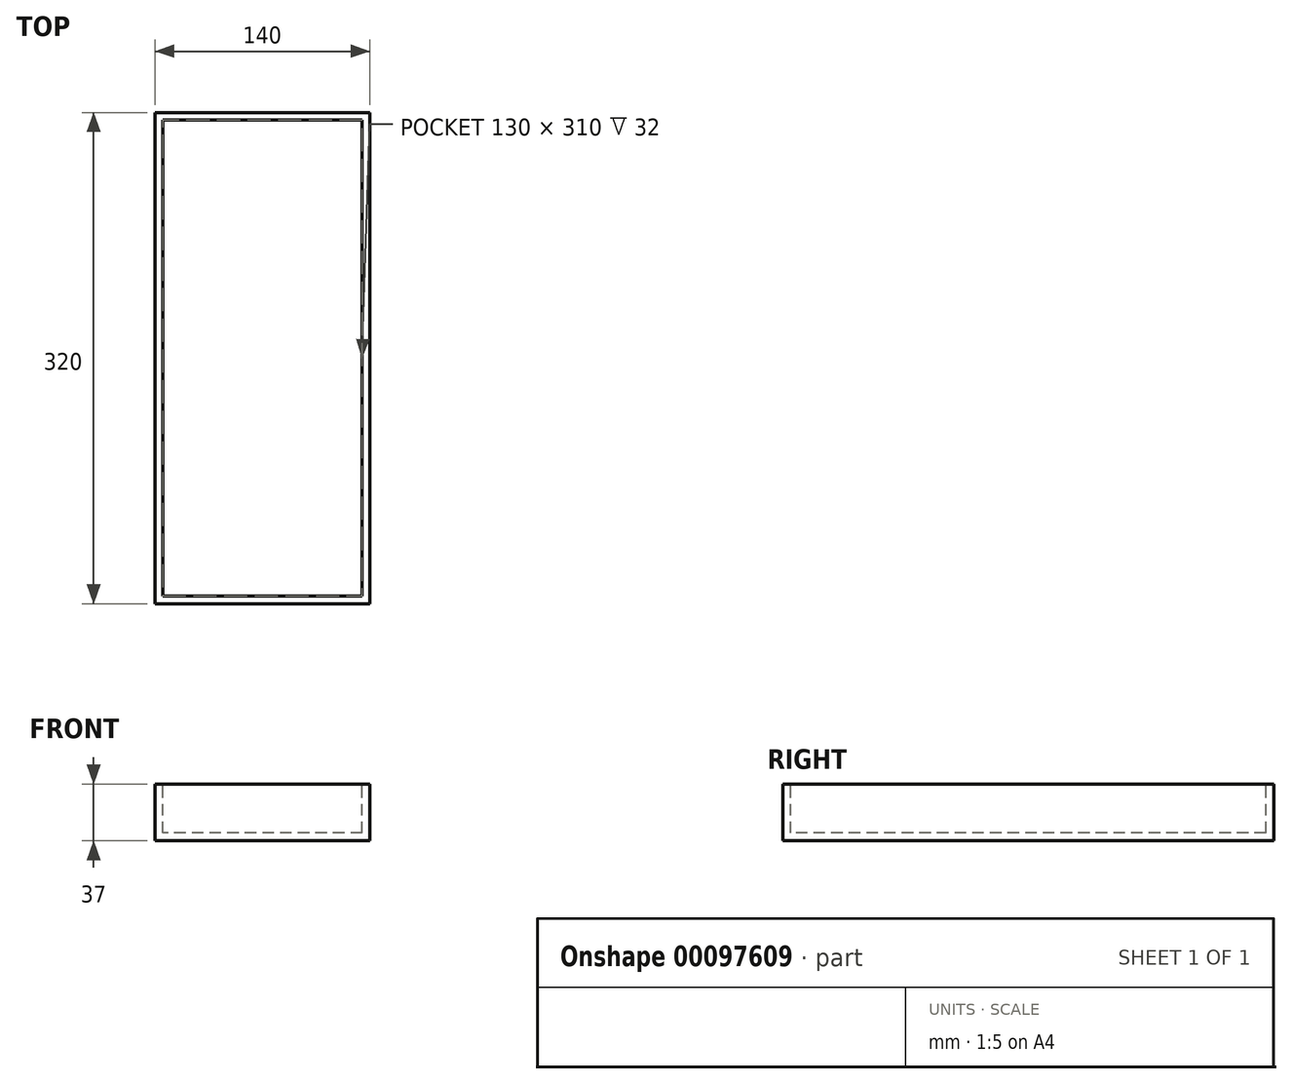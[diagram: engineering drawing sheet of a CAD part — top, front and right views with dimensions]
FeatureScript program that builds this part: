
annotation { "Feature Type Name" : "Feature", "Feature Type Description" : "" }
export const myFeature = defineFeature(function(context is Context, id is Id, definition is map)
    precondition{}
    {
        {
            var Q0;
            Q0=qCreatedBy(makeId("Top.planeOp"),FACE);
            var sketch = newSketch(context, id + "F0", { "sketchPlane" : qUnion([Q0])});
            skLineSegment(sketch, "E0.bottom", {"start": v(70, 160) * mm, "end": v(-70, 160) * mm});
            skLineSegment(sketch, "E0.top", {"start": v(70, -160) * mm, "end": v(-70, -160) * mm});
            skLineSegment(sketch, "E0.left", {"start": v(70, 160) * mm, "end": v(70, -160) * mm});
            skLineSegment(sketch, "E0.right", {"start": v(-70, 160) * mm, "end": v(-70, -160) * mm});
            skPoint(sketch, "E0.middle", {"position": v(0, 0) * mm});
            skSolve(sketch);
        }
        {
            var Q0;
            Q0 = qSketchRegion(id + "F0", true);
            extrude(context, id + "F1", {"entities" : qUnion([Q0]), "oppositeDirection" : true, "depth" : 37 * mm});
        }
        {
            var Q0;
            Q0=makeQuery(id+"F1.opExtrude","CAP_FACE",FACE,{"disambiguationData":[OSD([sQuery(id+"F0.wireOp",EDGE,"E0.bottom"),sQuery(id+"F0.wireOp",EDGE,"E0.top"),sQuery(id+"F0.wireOp",EDGE,"E0.left"),sQuery(id+"F0.wireOp",EDGE,"E0.right")])],"isStart":true});
            shell(context, id + "F2", {"entities" : qUnion([Q0]), "thickness" : 5 * mm});
        }
    });
